# Revit family: Hager-UNIVERS-Hollow_wall-IP30-With_Cover-With_DIN-NoHosted-CH-it
name_source: partatom
category: Electrical Equipment
units: mm (PartAtom-declared; Revit-internal decimal feet)

## family parameters
Always vertical = Yes
Cut with Voids When Loaded = No
Maintain Annotation Orientation = No
Panel Configuration = Two Columns, Circuits Across
Part Type = Panelboard
Room Calculation Point = No
Round Connector Dimension = Use Diameter
Shared = No
Work Plane-Based = Yes

## types (15) — shared parameters
Code hager = ADD-EC000214_EU
Default Elevation = 1200 mm
EF000003 - modo di montaggio = parete forata
EF000007 - colore = bianco
EF000024 - resistente ai raggi UV = No
EF000049 - profondità = 125 mm  [stored 0.410105 ft]
EF000116 - numero RAL = 9010
EF000118 - con piastra di montaggio = No
EF000218 - profondità di montaggio = 112 mm  [stored 0.367454 ft]
EF001062 - versione EMC = No
EF001088 - possibilità di applicazione = Yes
EF001134 - barra DIN = Yes
EF002950 - numero di unità modulari = 12
EF004462 - tipo di chiusura = altri
EF005474 - grado di protezione (IP) = IP30
EF006244 - coperchio/porta trasparente = No
EF006306 - con serratura = No
EF009212 - tipo di coperchio = con taglio
EF015776 - morsetto di messa a terra = No
EF015777 - morsettiera a conduttore neutro = No
EF015941 - porta di trasmissione del segnale = No
ETIM class code = EC000214
ETIM class name = Small distribution board
HG000002-with door or cover-it = Yes
HG000003-Range-it = UNIVERS
HG000005-Thickness-it = 2 mm  [stored 0.00656168 ft]
HG000006-Flush mounted-it = Yes
HG000011-Empty rows from bottom-it = No
HG000012-Door swing angle-it = 90.00°
HG000013-Door on the left-it = No
HG000014-Door on the right-it = Yes
HG000015-Clearance visibility-it = Yes
HG000016-Door 3D visibility-it = Yes
HG000017-Distance between poles-it = 18 mm  [stored 0.0590551 ft]
HG000060-RAL-number = 9010
HG000099-Onfly Template ID-it-CH = 507532
HGEF0002950-larghezza in unità di suddivisione = 12
Manufacturer = Hager
Name BIM&CO = Electricity
Name hager = ADD_Enclosures_EC000214
Reference = Template-Enclosure_EU-EC000214
Uniformat = Low Tension Service & Dist.
Uniformat code = D501001
zero-valued in all types: EF001131 - profondità interna, HG000007-Number of empty columns-it, HG000008-Number of empty rows-it

## per-type parameters (varying)
| type | BC_METADATA | EF000008 - larghezza | EF000040 - altezza | EF000266 - numero di file | EF000332 - altezza di installazione | EF000846 - larghezza di montaggio | HG000001 - Numero di colonne | HG000004-Manufacturer reference-it | HG000009-Double swing door-it | HG000010-Asymmetric doors-it | HGEF000266-Numero di file |
| UNIVERS-Hollow_wall_W353_H553_D125_12_Modular_Spacing-FWU31S1 | {"ObjectGuid":"cbcb2bb4-8450-4660-87c8-aeedd68d3e38","ModelGuid":"a1c422bb-80ab-4c67-b9f0-028bb5bdbd17","VariantGuid":"6ac08c7c-8903-4b29-85c8-32118dc360a9","Revision":"#47","VariantName":"UNIVERS-Hollow_wall_W353_H553_D125_12_Modular_Spacing-FWU31S1"} | 353 mm  [stored 1.15814 ft] | 553 mm  [stored 1.8143 ft] | 3 | 502 mm  [stored 1.64698 ft] | 310 mm  [stored 1.01706 ft] | 1 | FWU31S1 | No | No | 3 |
| UNIVERS-Hollow_wall_W603_H553_D125_12_Modular_Spacing-FWU32S1 | {"ObjectGuid":"cbcb2bb4-8450-4660-87c8-aeedd68d3e38","ModelGuid":"a1c422bb-80ab-4c67-b9f0-028bb5bdbd17","VariantGuid":"d34c8536-f116-481a-9e72-e738d85302d7","Revision":"#47","VariantName":"UNIVERS-Hollow_wall_W603_H553_D125_12_Modular_Spacing-FWU32S1"} | 603 mm | 553 mm  [stored 1.8143 ft] | 3 | 502 mm  [stored 1.64698 ft] | 560 mm  [stored 1.83727 ft] | 2 | FWU32S1 | No | No | 3 |
| UNIVERS-Hollow_wall_W853_H553_D125_12_Modular_Spacing-FWU33S1 | {"ObjectGuid":"cbcb2bb4-8450-4660-87c8-aeedd68d3e38","ModelGuid":"a1c422bb-80ab-4c67-b9f0-028bb5bdbd17","VariantGuid":"3c55ba67-abaa-4134-b759-21c4449cd233","Revision":"#47","VariantName":"UNIVERS-Hollow_wall_W853_H553_D125_12_Modular_Spacing-FWU33S1"} | 853 mm  [stored 2.79856 ft] | 553 mm  [stored 1.8143 ft] | 3 | 502 mm  [stored 1.64698 ft] | 810 mm | 3 | FWU33S1 | Yes | Yes | 3 |
| UNIVERS-Hollow_wall_W353_H703_D125_12_Modular_Spacing-FWU41S1 | {"ObjectGuid":"cbcb2bb4-8450-4660-87c8-aeedd68d3e38","ModelGuid":"a1c422bb-80ab-4c67-b9f0-028bb5bdbd17","VariantGuid":"22f4ffe1-ffe1-4ff1-9286-450bb669f0c4","Revision":"#47","VariantName":"UNIVERS-Hollow_wall_W353_H703_D125_12_Modular_Spacing-FWU41S1"} | 353 mm  [stored 1.15814 ft] | 703 mm  [stored 2.30643 ft] | 4 | 652 mm  [stored 2.13911 ft] | 310 mm  [stored 1.01706 ft] | 1 | FWU41S1 | No | No | 4 |
| UNIVERS-Hollow_wall_W603_H703_D125_12_Modular_Spacing-FWU42S1 | {"ObjectGuid":"cbcb2bb4-8450-4660-87c8-aeedd68d3e38","ModelGuid":"a1c422bb-80ab-4c67-b9f0-028bb5bdbd17","VariantGuid":"68a3674c-c03c-45be-8acc-546c64325002","Revision":"#47","VariantName":"UNIVERS-Hollow_wall_W603_H703_D125_12_Modular_Spacing-FWU42S1"} | 603 mm | 703 mm  [stored 2.30643 ft] | 4 | 652 mm  [stored 2.13911 ft] | 560 mm  [stored 1.83727 ft] | 2 | FWU42S1 | No | No | 4 |
| UNIVERS-Hollow_wall_W853_H703_D125_12_Modular_Spacing-FWU43S1 | {"ObjectGuid":"cbcb2bb4-8450-4660-87c8-aeedd68d3e38","ModelGuid":"a1c422bb-80ab-4c67-b9f0-028bb5bdbd17","VariantGuid":"5072172e-be06-4919-8451-ccd63984e8ff","Revision":"#47","VariantName":"UNIVERS-Hollow_wall_W853_H703_D125_12_Modular_Spacing-FWU43S1"} | 853 mm  [stored 2.79856 ft] | 703 mm  [stored 2.30643 ft] | 4 | 652 mm  [stored 2.13911 ft] | 810 mm | 3 | FWU43S1 | Yes | Yes | 4 |
| UNIVERS-Hollow_wall_W353_H853_D125_12_Modular_Spacing-FWU51S1 | {"ObjectGuid":"cbcb2bb4-8450-4660-87c8-aeedd68d3e38","ModelGuid":"a1c422bb-80ab-4c67-b9f0-028bb5bdbd17","VariantGuid":"9a240799-f26e-435f-9c63-b35aab201bbe","Revision":"#47","VariantName":"UNIVERS-Hollow_wall_W353_H853_D125_12_Modular_Spacing-FWU51S1"} | 353 mm  [stored 1.15814 ft] | 853 mm  [stored 2.79856 ft] | 5 | 802 mm  [stored 2.63123 ft] | 310 mm  [stored 1.01706 ft] | 1 | FWU51S1 | No | No | 5 |
| UNIVERS-Hollow_wall_W603_H853_D125_12_Modular_Spacing-FWU52S1 | {"ObjectGuid":"cbcb2bb4-8450-4660-87c8-aeedd68d3e38","ModelGuid":"a1c422bb-80ab-4c67-b9f0-028bb5bdbd17","VariantGuid":"fecd4f87-5cb9-458a-b036-d96ae8531d34","Revision":"#47","VariantName":"UNIVERS-Hollow_wall_W603_H853_D125_12_Modular_Spacing-FWU52S1"} | 603 mm | 853 mm  [stored 2.79856 ft] | 5 | 802 mm  [stored 2.63123 ft] | 560 mm  [stored 1.83727 ft] | 2 | FWU52S1 | No | No | 5 |
| UNIVERS-Hollow_wall_W853_H853_D125_12_Modular_Spacing-FWU53S1 | {"ObjectGuid":"cbcb2bb4-8450-4660-87c8-aeedd68d3e38","ModelGuid":"a1c422bb-80ab-4c67-b9f0-028bb5bdbd17","VariantGuid":"af75fafa-ecf1-4907-afd7-e24217756f50","Revision":"#47","VariantName":"UNIVERS-Hollow_wall_W853_H853_D125_12_Modular_Spacing-FWU53S1"} | 853 mm  [stored 2.79856 ft] | 853 mm  [stored 2.79856 ft] | 5 | 802 mm  [stored 2.63123 ft] | 810 mm | 3 | FWU53S1 | Yes | Yes | 5 |
| UNIVERS-Hollow_wall_W353_H1003_D125_12_Modular_Spacing-FWU61S1 | {"ObjectGuid":"cbcb2bb4-8450-4660-87c8-aeedd68d3e38","ModelGuid":"a1c422bb-80ab-4c67-b9f0-028bb5bdbd17","VariantGuid":"d7b56f06-6144-4bdf-971c-f83a299fad13","Revision":"#47","VariantName":"UNIVERS-Hollow_wall_W353_H1003_D125_12_Modular_Spacing-FWU61S1"} | 353 mm  [stored 1.15814 ft] | 1003 mm  [stored 3.29068 ft] | 6 | 952 mm  [stored 3.12336 ft] | 310 mm  [stored 1.01706 ft] | 1 | FWU61S1 | No | No | 6 |
| UNIVERS-Hollow_wall_W603_H1003_D125_12_Modular_Spacing-FWU62S1 | {"ObjectGuid":"cbcb2bb4-8450-4660-87c8-aeedd68d3e38","ModelGuid":"a1c422bb-80ab-4c67-b9f0-028bb5bdbd17","VariantGuid":"46cb6a3f-e9b5-4547-8cee-6df5399b1014","Revision":"#47","VariantName":"UNIVERS-Hollow_wall_W603_H1003_D125_12_Modular_Spacing-FWU62S1"} | 603 mm | 1003 mm  [stored 3.29068 ft] | 6 | 952 mm  [stored 3.12336 ft] | 560 mm  [stored 1.83727 ft] | 2 | FWU62S1 | No | No | 6 |
| UNIVERS-Hollow_wall_W853_H1003_D125_12_Modular_Spacing-FWU63S1 | {"ObjectGuid":"cbcb2bb4-8450-4660-87c8-aeedd68d3e38","ModelGuid":"a1c422bb-80ab-4c67-b9f0-028bb5bdbd17","VariantGuid":"ed9ac942-97ef-488a-a8ae-9fead353f5d0","Revision":"#47","VariantName":"UNIVERS-Hollow_wall_W853_H1003_D125_12_Modular_Spacing-FWU63S1"} | 853 mm  [stored 2.79856 ft] | 1003 mm  [stored 3.29068 ft] | 6 | 952 mm  [stored 3.12336 ft] | 810 mm | 3 | FWU63S1 | Yes | Yes | 6 |
| UNIVERS-Hollow_wall_W353_H1153_D125_12_Modular_Spacing-FWU71S1 | {"ObjectGuid":"cbcb2bb4-8450-4660-87c8-aeedd68d3e38","ModelGuid":"a1c422bb-80ab-4c67-b9f0-028bb5bdbd17","VariantGuid":"317ced8c-3ca6-419f-81eb-69bd3003c6f7","Revision":"#47","VariantName":"UNIVERS-Hollow_wall_W353_H1153_D125_12_Modular_Spacing-FWU71S1"} | 353 mm  [stored 1.15814 ft] | 1153 mm | 7 | 1102 mm  [stored 3.61549 ft] | 310 mm  [stored 1.01706 ft] | 1 | FWU71S1 | No | No | 7 |
| UNIVERS-Hollow_wall_W603_H1153_D125_12_Modular_Spacing-FWU72S1 | {"ObjectGuid":"cbcb2bb4-8450-4660-87c8-aeedd68d3e38","ModelGuid":"a1c422bb-80ab-4c67-b9f0-028bb5bdbd17","VariantGuid":"34815629-dcbf-40e8-93da-274999ff6721","Revision":"#47","VariantName":"UNIVERS-Hollow_wall_W603_H1153_D125_12_Modular_Spacing-FWU72S1"} | 603 mm | 1153 mm | 7 | 1102 mm  [stored 3.61549 ft] | 560 mm  [stored 1.83727 ft] | 2 | FWU72S1 | No | No | 7 |
| UNIVERS-Hollow_wall_W853_H1153_D125_12_Modular_Spacing-FWU73S1 | {"ObjectGuid":"cbcb2bb4-8450-4660-87c8-aeedd68d3e38","ModelGuid":"a1c422bb-80ab-4c67-b9f0-028bb5bdbd17","VariantGuid":"ed2445b9-8fe1-471d-a1e1-b11dadf535d4","Revision":"#47","VariantName":"UNIVERS-Hollow_wall_W853_H1153_D125_12_Modular_Spacing-FWU73S1"} | 853 mm  [stored 2.79856 ft] | 1153 mm | 7 | 1102 mm  [stored 3.61549 ft] | 810 mm | 3 | FWU73S1 | Yes | Yes | 7 |

note: [stored X ft] marks values corroborated as IEEE doubles in the binary element streams (Revit-internal decimal feet)

## geometry (parser evidence)
native form markers: Sweep x15
no freeform markers — native parametric forms only
